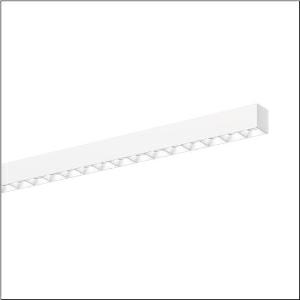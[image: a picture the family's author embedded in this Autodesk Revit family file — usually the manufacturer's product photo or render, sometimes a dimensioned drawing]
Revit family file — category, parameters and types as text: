
# Revit family: silica_r__21_51mx26da34wb_607f
name_source: partatom
category: Lighting Fixtures
units: mm (PartAtom-declared; Revit-internal decimal feet)

## family parameters
Cut with Voids When Loaded = No
Host = Face
Light Source = No
Part Type = Normal
Room Calculation Point = No
Round Connector Dimension = Use Diameter
Shared = No

## types (1)
- --- (1 x LED, 4320 lm, 25.1 W, 3000K)
    Apparent Load = 25 VA
    CIE Flux Codes = 83 98 100 100 100
    Color Rendering = 80
    Color Temperature = 3000K
    Default Elevation = 1800 mm
    Description = Silica® 21, office luminaire, primary light control with darklight reflector, of PMMA, white, CAT 2 (L<= 3000cd/m²), light emission: direct distribution, primary light characteristic: symmetric, installation type: surface-mounted, LED, rated luminous flux: 4.320lm, luminous efficacy: 172lm/W, light colour: 830, colour temperature: 3000K, with terminal, 3+2-pole, max. 2.5mm², mains connection: 220..240V, AC, 50/60Hz, rated input power: 25.1W, luminaire housing, of aluminium, traffic white (RAL 9016), length: 1.204mm, width: 53mm, height: 53mm, protection rating (complete): IP20, insulation class (complete): insulation class I (protective earthing), certification: CE, permissible operating ambient temperature: 0..+35°C, standard: EN 50419, packaging unit: 1 piece
    Height = 0 mm  [stored 0 ft]
    Lamp = 1 x LED
    Lamp Light Flux = 4320 lm
    Lamp Power = 25.1 W
    Lamp count = 1
    Length = 1204 mm
    Luminous efficacy = 172 lm/W
    Manufacturer = Siteco
    ModVariant = No
    Model = 51MX26DA34WB
    Mounting Place = Ceiling
    Mounting Type = Recessed
    Number of Poles = 1
    OnlyDefault = Yes
    Power Factor = 1
    Product Name = Silica® 21
    Product group = office luminaire | ceiling recessed
    ProductGroupID = 400
    Protection Class = Protection class I
    Protection Degree = IP 20
    RLX_Detail_Level = 1
    RLX_Emergency_Light_Flux = 0 lm
    RLX_Emergency_Type = 0
    RLX_Emergency_Type_DB = No
    RlxData = <blob elided: 38445 chars, md5=7829faf9>
    Socket = socket
    Standby Power = 0 W
    System Light Flux = 4320 lm
    System Power = 25 W
    Type Comments = factory setting: luminous flux: 100 % | dim-lin: 254 | 360 mA
    Type Image = l_1335934.jpg
    URL = http://relux.com
    VarID = @adj_094259
    Voltage = 0 V
    Weight = 0.00 kg
    Width = 53 mm

note: [stored X ft] marks values corroborated as IEEE doubles in the binary element streams (Revit-internal decimal feet)

## geometry (parser evidence)
native form markers: Blend x4, Sweep x10
no freeform markers — native parametric forms only
